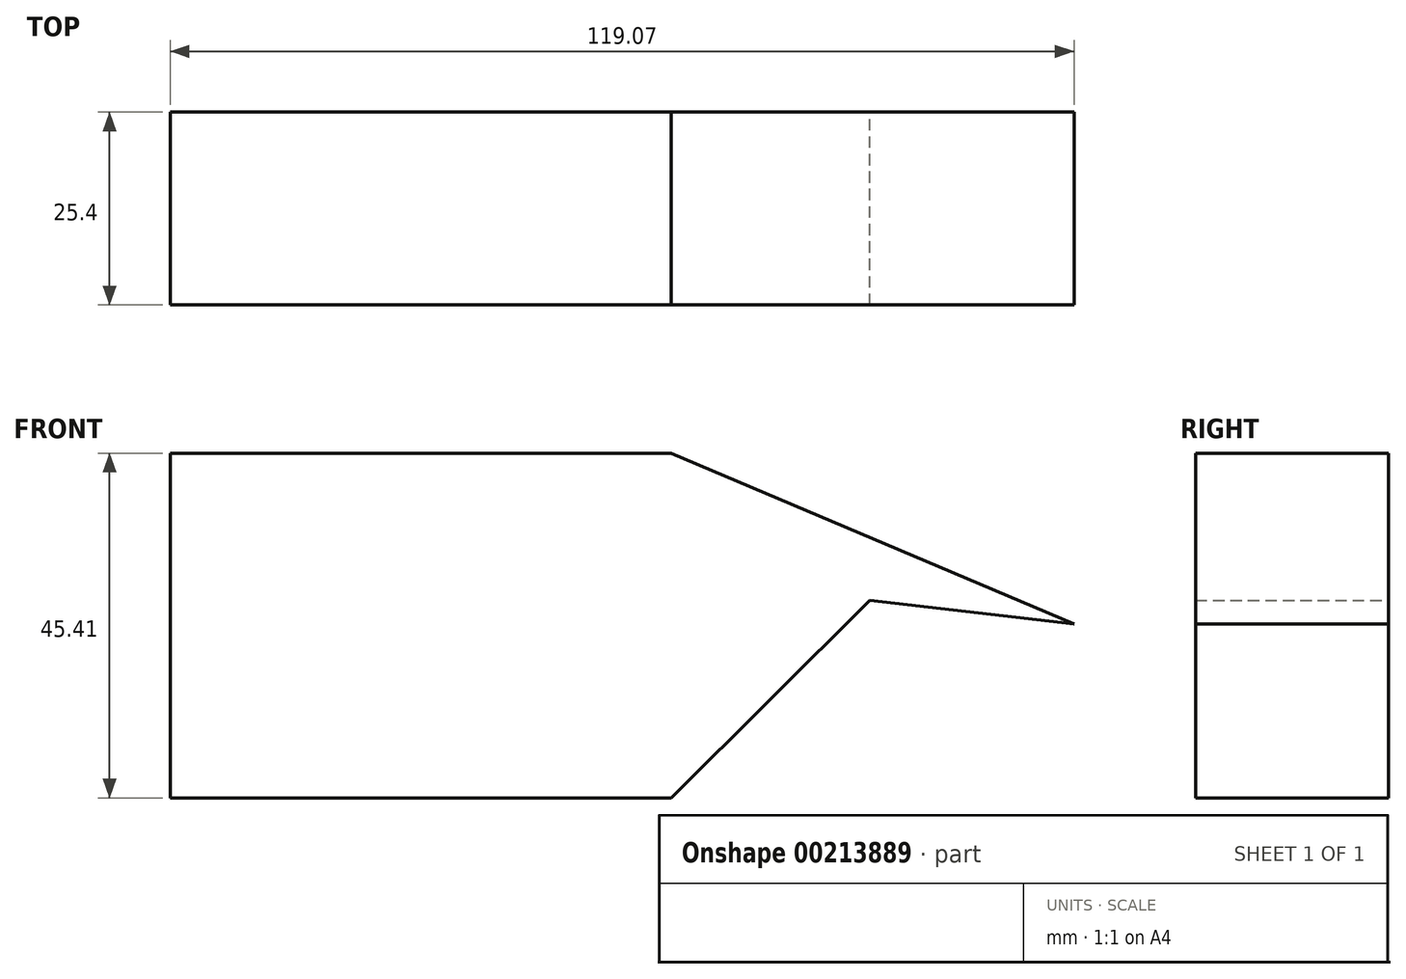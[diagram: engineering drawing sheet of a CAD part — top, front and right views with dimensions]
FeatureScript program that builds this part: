
annotation { "Feature Type Name" : "Feature", "Feature Type Description" : "" }
export const myFeature = defineFeature(function(context is Context, id is Id, definition is map)
    precondition{}
    {
        {
            var Q0;
            Q0=qCreatedBy(makeId("Front.planeOp"),FACE);
            var sketch = newSketch(context, id + "F0", { "sketchPlane" : qUnion([Q0])});
            skLineSegment(sketch, "E0", {"start": v(0, 0) * mm, "end": v(-65.98, 0) * mm});
            skLineSegment(sketch, "E1", {"start": v(-65.98, 0) * mm, "end": v(-65.98, 45.4) * mm});
            skLineSegment(sketch, "E2", {"start": v(-65.98, 45.4) * mm, "end": v(0, 45.4) * mm});
            skLineSegment(sketch, "E3", {"start": v(0, 45.4) * mm, "end": v(0, 0) * mm});
            skLineSegment(sketch, "E4", {"start": v(0, 45.4) * mm, "end": v(53.1, 22.93) * mm});
            skLineSegment(sketch, "E5", {"start": v(0, 0) * mm, "end": v(40.88, 40.63) * mm});
            skLineSegment(sketch, "E6", {"start": v(13.96, 27.42) * mm, "end": v(53.1, 22.93) * mm});
            skSolve(sketch);
        }
        {
            var Q0;
            Q0 = qSketchRegion(id + "F0", true);
            extrude(context, id + "F1", {"entities" : qUnion([Q0]), "depth" : 25.4 * mm});
        }
    });
